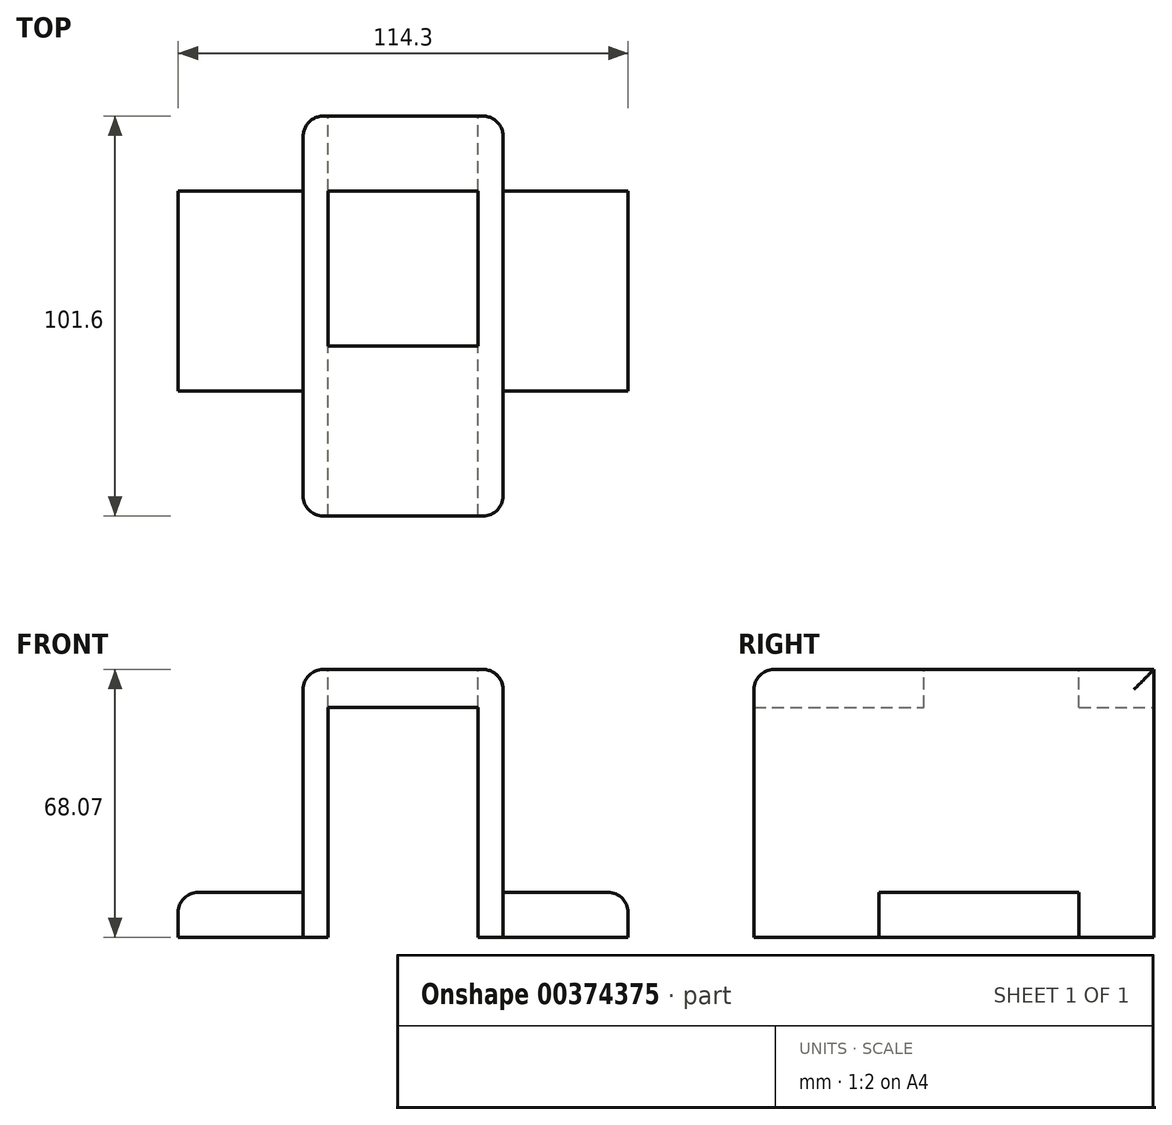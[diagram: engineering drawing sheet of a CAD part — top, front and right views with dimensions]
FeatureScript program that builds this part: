
annotation { "Feature Type Name" : "Feature", "Feature Type Description" : "" }
export const myFeature = defineFeature(function(context is Context, id is Id, definition is map)
    precondition{}
    {
        {
            var Q0;
            Q0=qCreatedBy(makeId("Top.planeOp"),FACE);
            var sketch = newSketch(context, id + "F0", { "sketchPlane" : qUnion([Q0])});
            skLineSegment(sketch, "E0.bottom", {"start": v(0, 0) * mm, "end": v(38.1, 0) * mm});
            skLineSegment(sketch, "E0.top", {"start": v(0, 88.9) * mm, "end": v(38.1, 88.9) * mm});
            skLineSegment(sketch, "E0.left", {"start": v(0, 0) * mm, "end": v(0, 88.9) * mm});
            skLineSegment(sketch, "E0.right", {"start": v(38.1, 0) * mm, "end": v(38.1, 88.9) * mm});
            skLineSegment(sketch, "E1", {"start": v(0, 36.83) * mm, "end": v(38.1, 36.83) * mm});
            skLineSegment(sketch, "E2", {"start": v(0, 76.2) * mm, "end": v(38.1, 76.2) * mm});
            skLineSegment(sketch, "E3", {"start": v(0, 88.9) * mm, "end": v(38.1, 0) * mm, "construction": true});
            skLineSegment(sketch, "E4", {"start": v(38.1, 88.9) * mm, "end": v(0, 0) * mm, "construction": true});
            skLineSegment(sketch, "E5.bottom", {"start": v(44.45, 95.25) * mm, "end": v(-6.35, 95.25) * mm});
            skLineSegment(sketch, "E5.top", {"start": v(44.45, -6.35) * mm, "end": v(-6.35, -6.35) * mm});
            skLineSegment(sketch, "E5.left", {"start": v(44.45, 95.25) * mm, "end": v(44.45, -6.35) * mm});
            skLineSegment(sketch, "E5.right", {"start": v(-6.35, 95.25) * mm, "end": v(-6.35, -6.35) * mm});
            skPoint(sketch, "E5.middle", {"position": v(19.05, 44.45) * mm});
            skSolve(sketch);
        }
        {
            var Q0;
            {var subQ6=sQuery(id+"F0.wireOp",EDGE,"E0.bottom");Q0=makeQuery(id+"F0.imprint","IMPRINT",FACE,{"disambiguationData":[TD([[makeQuery(id+"F0.imprint","IMPRINT",EDGE,{"derivedFrom":subQ6}),-1.0]])]});}
            var Q1;
            {var subQ0=sQuery(id+"F0.wireOp",EDGE,"E0.top");Q1=makeQuery(id+"F0.imprint","IMPRINT",FACE,{"disambiguationData":[TD([[makeQuery(id+"F0.imprint","IMPRINT",EDGE,{"derivedFrom":subQ0}),-1.0]])]});}
            var Q2;
            {var subQ0=sQuery(id+"F0.wireOp",EDGE,"E0.bottom");Q2=makeQuery(id+"F0.imprint","IMPRINT",FACE,{"disambiguationData":[TD([[makeQuery(id+"F0.imprint","IMPRINT",EDGE,{"derivedFrom":subQ0}),1.0]])]});}
            extrude(context, id + "F1", {"entities" : qUnion([Q0, Q1, Q2]), "oppositeDirection" : true, "depth" : 9.65 * mm});
        }
        {
            var Q0;
            Q0=makeQuery(id+"F1.opExtrude","CAP_FACE",FACE,{"disambiguationData":[OSD([sQuery(id+"F0.wireOp",EDGE,"E0.left"),sQuery(id+"F0.wireOp",EDGE,"E0.right"),sQuery(id+"F0.wireOp",EDGE,"E1"),sQuery(id+"F0.wireOp",EDGE,"E2"),sQuery(id+"F0.wireOp",EDGE,"E5.bottom"),sQuery(id+"F0.wireOp",EDGE,"E5.top"),sQuery(id+"F0.wireOp",EDGE,"E5.left"),sQuery(id+"F0.wireOp",EDGE,"E5.right")])],"isStart":false});
            var sketch = newSketch(context, id + "F2", { "sketchPlane" : qUnion([Q0])});
            skLineSegment(sketch, "E6.bottom", {"start": v(-6.35, 6.35) * mm, "end": v(44.45, 6.35) * mm});
            skLineSegment(sketch, "E6.top", {"start": v(-6.35, -95.25) * mm, "end": v(44.45, -95.25) * mm});
            skLineSegment(sketch, "E6.left", {"start": v(-6.35, 6.35) * mm, "end": v(-6.35, -95.25) * mm});
            skLineSegment(sketch, "E6.right", {"start": v(44.45, 6.35) * mm, "end": v(44.45, -95.25) * mm});
            skLineSegment(sketch, "E7.bottom", {"start": v(0, 0) * mm, "end": v(38.1, 0) * mm});
            skLineSegment(sketch, "E7.top", {"start": v(0, -88.9) * mm, "end": v(38.1, -88.9) * mm});
            skLineSegment(sketch, "E7.left", {"start": v(0, 0) * mm, "end": v(0, -88.9) * mm});
            skLineSegment(sketch, "E7.right", {"start": v(38.1, 0) * mm, "end": v(38.1, -88.9) * mm});
            skSolve(sketch);
        }
        {
            var Q0;
            Q0=makeQuery(id+"F2.imprint","IMPRINT",FACE,{"disambiguationData":[TD([[makeQuery(id+"F2.imprint","IMPRINT",EDGE,{"derivedFrom":sQuery(id+"F2.wireOp",EDGE,"E6.bottom")}),1.0]])]});
            extrude(context, id + "F3", {"entities" : qUnion([Q0]), "operationType" : NewBodyOperationType.ADD, "depth" : 58.42 * mm});
        }
        {
            var Q0;
            Q0=makeQuery(id+"F3.opExtrude","CAP_FACE",FACE,{"disambiguationData":[OSD([sQuery(id+"F2.wireOp",EDGE,"E6.bottom"),sQuery(id+"F2.wireOp",EDGE,"E6.top"),sQuery(id+"F2.wireOp",EDGE,"E6.left"),sQuery(id+"F2.wireOp",EDGE,"E6.right"),sQuery(id+"F2.wireOp",EDGE,"E7.bottom"),sQuery(id+"F2.wireOp",EDGE,"E7.top"),sQuery(id+"F2.wireOp",EDGE,"E7.left"),sQuery(id+"F2.wireOp",EDGE,"E7.right")])],"isStart":false});
            var sketch = newSketch(context, id + "F4", { "sketchPlane" : qUnion([Q0])});
            skLineSegment(sketch, "E8.bottom", {"start": v(0, -25.4) * mm, "end": v(-38.1, -25.4) * mm});
            skLineSegment(sketch, "E8.top", {"start": v(0, -76.2) * mm, "end": v(-38.1, -76.2) * mm});
            skLineSegment(sketch, "E8.left", {"start": v(0, -25.4) * mm, "end": v(0, -76.2) * mm});
            skLineSegment(sketch, "E8.right", {"start": v(-38.1, -25.4) * mm, "end": v(-38.1, -76.2) * mm});
            skLineSegment(sketch, "E9.bottom", {"start": v(38.1, -25.4) * mm, "end": v(76.2, -25.4) * mm});
            skLineSegment(sketch, "E9.top", {"start": v(38.1, -76.2) * mm, "end": v(76.2, -76.2) * mm});
            skLineSegment(sketch, "E9.left", {"start": v(38.1, -25.4) * mm, "end": v(38.1, -76.2) * mm});
            skLineSegment(sketch, "E9.right", {"start": v(76.2, -25.4) * mm, "end": v(76.2, -76.2) * mm});
            skSolve(sketch);
        }
        {
            var Q0;
            {var subQ0=sQuery(id+"F4.wireOp",EDGE,"E9.right");Q0=makeQuery(id+"F4.imprint","IMPRINT",FACE,{"disambiguationData":[TD([[makeQuery(id+"F4.imprint","IMPRINT",EDGE,{"derivedFrom":subQ0}),-1.0]])]});}
            var Q1;
            {var subQ0=sQuery(id+"F4.wireOp",EDGE,"E8.right");Q1=makeQuery(id+"F4.imprint","IMPRINT",FACE,{"disambiguationData":[TD([[makeQuery(id+"F4.imprint","IMPRINT",EDGE,{"derivedFrom":subQ0}),1.0]])]});}
            extrude(context, id + "F5", {"entities" : qUnion([Q0, Q1]), "operationType" : NewBodyOperationType.ADD, "oppositeDirection" : true, "depth" : 11.43 * mm});
        }
        {
            var Q0;
            Q0=makeQuery(id+"F5.opExtrude","CAP_EDGE",EDGE,{"disambiguationData":[OSD([sQuery(id+"F4.wireOp",EDGE,"E8.right")])],"isStart":false});
            var Q1;
            Q1=makeQuery(id+"F5.opExtrude","CAP_EDGE",EDGE,{"disambiguationData":[OSD([sQuery(id+"F4.wireOp",EDGE,"E9.right")])],"isStart":false});
            fillet(context, id + "F6", {"entities" : qUnion([Q0, Q1]), "radius" : 5.08 * mm, "tangentPropagation" : true, "allowEdgeOverflow" : false});
        }
        {
            var Q0;
            Q0=makeQuery(id+"F3.boolean.opBoolean","MERGE",FACE,{"derivedFrom":[makeQuery(id+"F1.opExtrude","SWEPT_FACE",FACE,{"disambiguationData":[OSD([sQuery(id+"F0.wireOp",EDGE,"E5.top")])]}),makeQuery(id+"F3.opExtrude","SWEPT_FACE",FACE,{"disambiguationData":[OSD([sQuery(id+"F2.wireOp",EDGE,"E6.bottom")])]})]});
            var sketch = newSketch(context, id + "F7", { "sketchPlane" : qUnion([Q0])});
            skLineSegment(sketch, "E10.bottom", {"start": v(0, -9.65) * mm, "end": v(38.1, -9.65) * mm});
            skLineSegment(sketch, "E10.top", {"start": v(0, -68.07) * mm, "end": v(38.1, -68.07) * mm});
            skLineSegment(sketch, "E10.left", {"start": v(0, -9.65) * mm, "end": v(0, -68.07) * mm});
            skLineSegment(sketch, "E10.right", {"start": v(38.1, -9.65) * mm, "end": v(38.1, -68.07) * mm});
            skSolve(sketch);
        }
        {
            var Q0;
            Q0 = qSketchRegion(id + "F7", true);
            extrude(context, id + "F8", {"entities" : qUnion([Q0]), "operationType" : NewBodyOperationType.REMOVE, "endBound" : BoundingType.THROUGH_ALL, "oppositeDirection" : true, "depth" : 25.4 * mm});
        }
        {
            var Q0;
            Q0=makeQuery(id+"F1.opExtrude","CAP_EDGE",EDGE,{"disambiguationData":[OSD([sQuery(id+"F0.wireOp",EDGE,"E5.top")])],"isStart":true});
            var Q1;
            Q1=makeQuery(id+"F3.boolean.opBoolean","MERGE",EDGE,{"derivedFrom":[makeQuery(id+"F1.opExtrude","SWEPT_EDGE",EDGE,{"disambiguationData":[OSD([sQuery(id+"F0.wireOp",EDGE,"E5.top"),sQuery(id+"F0.wireOp",EDGE,"E5.left")])]}),makeQuery(id+"F3.opExtrude","SWEPT_EDGE",EDGE,{"disambiguationData":[OSD([sQuery(id+"F2.wireOp",EDGE,"E6.bottom"),sQuery(id+"F2.wireOp",EDGE,"E6.right")])]})]});
            var Q2;
            Q2=makeQuery(id+"F3.boolean.opBoolean","MERGE",EDGE,{"derivedFrom":[makeQuery(id+"F1.opExtrude","SWEPT_EDGE",EDGE,{"disambiguationData":[OSD([sQuery(id+"F0.wireOp",EDGE,"E5.top"),sQuery(id+"F0.wireOp",EDGE,"E5.right")])]}),makeQuery(id+"F3.opExtrude","SWEPT_EDGE",EDGE,{"disambiguationData":[OSD([sQuery(id+"F2.wireOp",EDGE,"E6.bottom"),sQuery(id+"F2.wireOp",EDGE,"E6.left")])]})]});
            var Q3;
            Q3=makeQuery(id+"F1.opExtrude","CAP_EDGE",EDGE,{"disambiguationData":[OSD([sQuery(id+"F0.wireOp",EDGE,"E5.left")])],"isStart":true});
            var Q4;
            Q4=makeQuery(id+"F1.opExtrude","CAP_EDGE",EDGE,{"disambiguationData":[OSD([sQuery(id+"F0.wireOp",EDGE,"E5.right")])],"isStart":true});
            var Q5;
            Q5=makeQuery(id+"F3.boolean.opBoolean","MERGE",EDGE,{"derivedFrom":[makeQuery(id+"F1.opExtrude","SWEPT_EDGE",EDGE,{"disambiguationData":[OSD([sQuery(id+"F0.wireOp",EDGE,"E5.bottom"),sQuery(id+"F0.wireOp",EDGE,"E5.left")])]}),makeQuery(id+"F3.opExtrude","SWEPT_EDGE",EDGE,{"disambiguationData":[OSD([sQuery(id+"F2.wireOp",EDGE,"E6.top"),sQuery(id+"F2.wireOp",EDGE,"E6.right")])]})]});
            var Q6;
            Q6=makeQuery(id+"F3.boolean.opBoolean","MERGE",EDGE,{"derivedFrom":[makeQuery(id+"F1.opExtrude","SWEPT_EDGE",EDGE,{"disambiguationData":[OSD([sQuery(id+"F0.wireOp",EDGE,"E5.bottom"),sQuery(id+"F0.wireOp",EDGE,"E5.right")])]}),makeQuery(id+"F3.opExtrude","SWEPT_EDGE",EDGE,{"disambiguationData":[OSD([sQuery(id+"F2.wireOp",EDGE,"E6.top"),sQuery(id+"F2.wireOp",EDGE,"E6.left")])]})]});
            fillet(context, id + "F9", {"entities" : qUnion([Q0, Q1, Q2, Q3, Q4, Q5, Q6]), "radius" : 5.08 * mm, "tangentPropagation" : true, "allowEdgeOverflow" : false});
        }
    });
